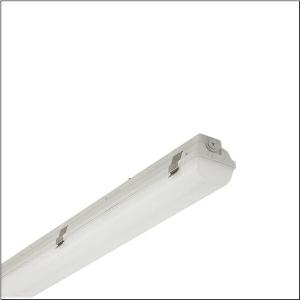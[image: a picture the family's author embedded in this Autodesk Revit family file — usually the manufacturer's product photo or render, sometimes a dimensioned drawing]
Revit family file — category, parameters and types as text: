
# Revit family: monsun_r__21_eco_51fj20ml45a_05e8
name_source: partatom
category: Lighting Fixtures
units: mm (PartAtom-declared; Revit-internal decimal feet)

## family parameters
Cut with Voids When Loaded = No
Host = Face
Light Source = No
Part Type = Normal
Room Calculation Point = No
Round Connector Dimension = Use Diameter
Shared = No

## types (1)
- --- (1 x LED, 4900 lm, 36 W, 4000K)
    Apparent Load = 36 VA
    CIE Flux Codes = 40 69 88 88 100
    Color Rendering = 80
    Color Temperature = 4000K
    Default Elevation = 1800 mm
    Description = Monsun® 21 Eco, damp-proof luminaire, primary optical cover: diffuser, of PC, UV-stabilised, frosted, light emission: direct distribution, primary light characteristic: symmetric, installation type: suspended mounting, surface-mounted, LED, rated luminous flux: 4.900lm, luminous efficacy: 132lm/W, light colour: 840, colour temperature: 4000K, control gear: ECG Multilumen, with terminal, 3-pole, max. 2.5mm², mains connection: 220..240V, AC, 50/60Hz, rated input power: 36W, housing, of glass-fibre reinforced polyester, light grey (RAL 7035), length: 1.277mm, width: 90mm, height: 95mm, clip for enclosure, of spring steel V2A, protection rating (complete): IP66, insulation class (complete): insulation class I (protective earthing), certification: CE, UKCA, protection symbol: D, impact resistance: IK08, permissible operating ambient temperature: -20..+35°C, corresponds to IFS (International Featured Standards) requirements for safety and quality in the food industry, contact your sales advisor before using the luminaires in applications with unclear chemical exposure, large temperature fluctuations or condensation-forming humidity, packaging unit: 1 piece
    Height = 103 mm
    Lamp = 1 x LED
    Lamp Light Flux = 4900 lm
    Lamp Power = 36 W
    Lamp count = 1
    Length = 1277 mm
    Luminous efficacy = 136 lm/W
    Manufacturer = Siteco
    ModVariant = No
    Model = 51FJ20ML45A
    Mounting Place = Ceiling
    Mounting Type = Surface mounted
    Number of Poles = 1
    OnlyDefault = Yes
    Power Factor = 1
    Product Name = Monsun® 21 Eco
    Product group = damp-proof luminaire
    ProductGroupID = 300
    Protection Class = Protection class I
    Protection Degree = IP 66
    RLX_Detail_Level = 1
    RLX_Emergency_Light_Flux = 0 lm
    RLX_Emergency_Type = 0
    RLX_Emergency_Type_DB = No
    RlxData = <blob elided: 34113 chars, md5=b2bb5cb0>
    Socket = socket
    Standby Power = 0 W
    System Light Flux = 4900 lm
    System Power = 36 W
    Type Comments = factory setting: luminous flux: 100 % | (ON | ON) | 350 mA
    Type Image = l_1007218.jpg
    URL = http://relux.com
    VarID = @adj_116115
    Voltage = 0 V
    Weight = 0.00 kg
    Width = 90 mm

## geometry (parser evidence)
native form markers: Blend x4, Sweep x11
no freeform markers — native parametric forms only
